# Revit family: Haworth_Solis Drum_Light_Small
name_source: partatom
category: Lighting Fixtures
revit_build: Autodesk Revit 2018 (Build: 20170223_1515(x64)
units: mm (PartAtom-declared; Revit-internal decimal feet)

## family parameters
Always vertical = Yes
Cut with Voids When Loaded = No
Light Source = Yes
OmniClass Number = 23.80.70.11.14
OmniClass Title = General Luminaries, Directional
Part Type = Normal
Room Calculation Point = No
Round Connector Dimension = Use Diameter
Shared = No
Work Plane-Based = No

## types (1)
- HCPL-SDP1-24
    Actual Depth = 24"
    Actual Height = 10"
    Actual Width = 24"
    Assembly Code = D5020200
    Base Radius = 11 221/256"
    Base Radius Extrusion = 11 115/128"
    Chrome Finish = Haworth _ Metal _ Chrome
    Color Filter = 16777215
    Cords Finish = Haworth _ Paint _ Metallic Silver
    Description = Haworth Solis Drum Light Small Pendant Light"
    Dimming Lamp Color Temperature Shift = Incandescent Lamp Curve
    Emit Shape Visible in Rendering = No
    Emit from Circle Diameter = 24"
    Glass Finish = Haworth _ Acrylic _ Clear
    Manufacturer = Haworth
    Model = HCPL-SDP1-24
    Photometric Web File = generic
    Revision Number = 1
    Size = Verify Final Dim. w/Haworth
    Tilt Angle = 90.00°
    Top Radius = 11 15/128"
    URL = https://www.haworth.com
    URL - Product = https://www.haworth.com
    Warranty = https://www.haworth.com
